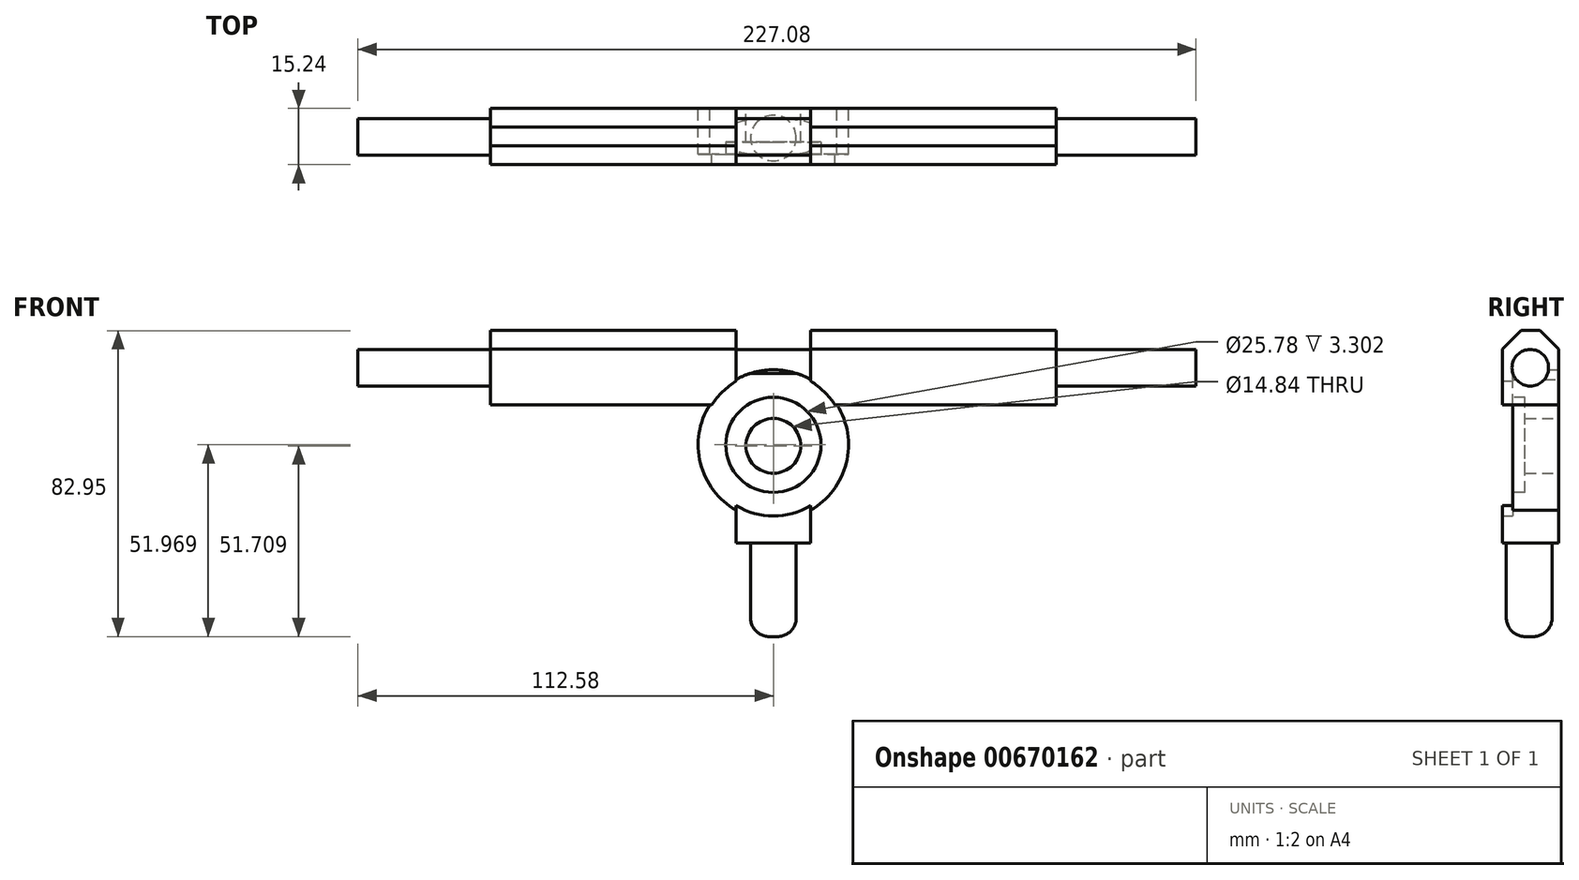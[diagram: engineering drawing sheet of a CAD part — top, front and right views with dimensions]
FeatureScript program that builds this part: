
annotation { "Feature Type Name" : "Feature", "Feature Type Description" : "" }
export const myFeature = defineFeature(function(context is Context, id is Id, definition is map)
    precondition{}
    {
        {
            var Q0;
            Q0=qCreatedBy(makeId("Front.planeOp"),FACE);
            var sketch = newSketch(context, id + "F0", { "sketchPlane" : qUnion([Q0])});
            skLineSegment(sketch, "E0.bottom", {"start": v(-76.65, -10.07) * mm, "end": v(76.65, -10.07) * mm});
            skLineSegment(sketch, "E0.top", {"start": v(-76.65, 10.07) * mm, "end": v(76.65, 10.07) * mm});
            skLineSegment(sketch, "E0.left", {"start": v(-76.65, -10.07) * mm, "end": v(-76.65, 10.07) * mm});
            skLineSegment(sketch, "E0.right", {"start": v(76.65, -10.07) * mm, "end": v(76.65, 10.07) * mm});
            skPoint(sketch, "E0.middle", {"position": v(0, 0) * mm});
            skLineSegment(sketch, "E1.bottom", {"start": v(-10.07, 10.07) * mm, "end": v(10.07, 10.07) * mm});
            skLineSegment(sketch, "E1.top", {"start": v(-10.07, -87.46) * mm, "end": v(10.07, -87.46) * mm});
            skLineSegment(sketch, "E1.left", {"start": v(-10.07, 10.07) * mm, "end": v(-10.07, -87.46) * mm});
            skLineSegment(sketch, "E1.right", {"start": v(10.07, 10.07) * mm, "end": v(10.07, -87.46) * mm});
            skPoint(sketch, "E1.middle", {"position": v(0, -38.7) * mm});
            skArc(sketch, "E2", {"start": v(0, -73.83) * mm, "mid": v(-26.8, -28.1) * mm, "end": v(-76.65, -10.07) * mm});
            skArc(sketch, "E3", {"start": v(76.65, -10.07) * mm, "mid": v(26.8, -28.1) * mm, "end": v(0, -73.83) * mm});
            skLineSegment(sketch, "E4", {"start": v(-10.07, -47.48) * mm, "end": v(10.07, -47.48) * mm});
            skCircle(sketch, "E5", {"center": v(0, -20.52) * mm, "radius": 19.66 * mm});
            skCircle(sketch, "E6", {"center": v(0, -20.52) * mm, "radius": 10.32 * mm});
            skSolve(sketch);
        }
        {
            var Q0;
            {var subQ5=sQuery(id+"F0.wireOp",EDGE,"E0.left");Q0=makeQuery(id+"F0.imprint","IMPRINT",FACE,{"disambiguationData":[TD([[makeQuery(id+"F0.imprint","IMPRINT",EDGE,{"derivedFrom":subQ5}),-1.0]])]});}
            var Q1;
            {var subQ1=sQuery(id+"F0.wireOp",EDGE,"E0.bottom");var subQ3=sQuery(id+"F0.wireOp",EDGE,"E5");var subQ4=makeQuery(id+"F0.imprint","INTERSECT",VERTEX,{"disambiguationData":[OD(0.0)],"derivedFrom":[subQ1,subQ3]});Q1=makeQuery(id+"F0.imprint","IMPRINT",FACE,{"disambiguationData":[TD([[makeQuery(id+"F0.imprint","IMPRINT",EDGE,{"disambiguationData":[TD([[subQ4,-1.0]])],"derivedFrom":subQ3}),-1.0]])]});}
            var Q2;
            {var subQ5=sQuery(id+"F0.wireOp",EDGE,"E0.right");Q2=makeQuery(id+"F0.imprint","IMPRINT",FACE,{"disambiguationData":[TD([[makeQuery(id+"F0.imprint","IMPRINT",EDGE,{"derivedFrom":subQ5}),1.0]])]});}
            var Q3;
            {var subQ1=sQuery(id+"F0.wireOp",EDGE,"E0.bottom");var subQ3=sQuery(id+"F0.wireOp",EDGE,"E5");var subQ4=makeQuery(id+"F0.imprint","INTERSECT",VERTEX,{"disambiguationData":[OD(1.0)],"derivedFrom":[subQ1,subQ3]});Q3=makeQuery(id+"F0.imprint","IMPRINT",FACE,{"disambiguationData":[TD([[makeQuery(id+"F0.imprint","IMPRINT",EDGE,{"disambiguationData":[TD([[subQ4,1.0]])],"derivedFrom":subQ3}),-1.0]])]});}
            var Q4;
            {var subQ0=sQuery(id+"F0.wireOp",EDGE,"E1.bottom");Q4=makeQuery(id+"F0.imprint","IMPRINT",FACE,{"disambiguationData":[TD([[makeQuery(id+"F0.imprint","IMPRINT",EDGE,{"derivedFrom":subQ0}),-1.0]])]});}
            var Q5;
            {var subQ0=sQuery(id+"F0.wireOp",EDGE,"E4");Q5=makeQuery(id+"F0.imprint","IMPRINT",FACE,{"disambiguationData":[TD([[makeQuery(id+"F0.imprint","IMPRINT",EDGE,{"derivedFrom":subQ0}),1.0]])]});}
            extrude(context, id + "F1", {"entities" : qUnion([Q0, Q1, Q2, Q3, Q4, Q5]), "depth" : 15.24 * mm, "offsetDistance" : 25.4 * mm});
        }
        {
            var Q0;
            Q0=makeQuery(id+"F1.opExtrude","SWEPT_FACE",FACE,{"disambiguationData":[OSD([sQuery(id+"F0.wireOp",EDGE,"E4")])]});
            var sketch = newSketch(context, id + "F2", { "sketchPlane" : qUnion([Q0])});
            skCircle(sketch, "E7", {"center": v(0, 8.03) * mm, "radius": 6.2 * mm});
            skSolve(sketch);
        }
        {
            var Q0;
            Q0 = qSketchRegion(id + "F2", true);
            extrude(context, id + "F3", {"entities" : qUnion([Q0]), "operationType" : NewBodyOperationType.ADD, "depth" : 25.4 * mm, "offsetDistance" : 25.4 * mm});
        }
        {
            var Q0;
            Q0=makeQuery(id+"F3.opExtrude","CAP_FACE",FACE,{"disambiguationData":[OSD([sQuery(id+"F2.wireOp",EDGE,"E7")])],"isStart":false});
            fillet(context, id + "F4", {"entities" : qUnion([Q0]), "radius" : 5.08 * mm, "tangentPropagation" : true, "allowEdgeOverflow" : false});
        }
        {
            var Q0;
            Q0=makeQuery(id+"F1.opExtrude","SWEPT_FACE",FACE,{"disambiguationData":[OSD([sQuery(id+"F0.wireOp",EDGE,"E0.right")])]});
            var sketch = newSketch(context, id + "F5", { "sketchPlane" : qUnion([Q0])});
            skCircle(sketch, "E8", {"center": v(-7.74, 0) * mm, "radius": 4.96 * mm});
            skSolve(sketch);
        }
        {
            var Q0;
            Q0=makeQuery(id+"F5.imprint","IMPRINT",FACE,{"disambiguationData":[TD([[makeQuery(id+"F5.imprint","IMPRINT",EDGE,{"derivedFrom":sQuery(id+"F5.wireOp",EDGE,"E8")}),1.0]])]});
            extrude(context, id + "F6", {"entities" : qUnion([Q0]), "depth" : 37.85 * mm, "offsetDistance" : 25.4 * mm, "hasSecondDirection" : true, "secondDirectionOppositeDirection" : true, "secondDirectionDepth" : 189.23 * mm});
        }
        {
            var Q0;
            Q0=qCreatedBy(makeId("Front.planeOp"),FACE);
            var sketch = newSketch(context, id + "F7", { "sketchPlane" : qUnion([Q0])});
            skCircle(sketch, "E9", {"center": v(0, -20.91) * mm, "radius": 20.37 * mm});
            skSolve(sketch);
        }
        {
            var Q0;
            Q0 = qSketchRegion(id + "F7", true);
            extrude(context, id + "F8", {"entities" : qUnion([Q0]), "operationType" : NewBodyOperationType.ADD, "depth" : 12.45 * mm, "offsetDistance" : 25.4 * mm});
        }
        {
            var Q0;
            Q0=makeQuery(id+"F8.opExtrude","CAP_FACE",FACE,{"disambiguationData":[OSD([sQuery(id+"F7.wireOp",EDGE,"E9")])],"isStart":false});
            var sketch = newSketch(context, id + "F9", { "sketchPlane" : qUnion([Q0])});
            skCircle(sketch, "E10", {"center": v(0, -20.91) * mm, "radius": 12.89 * mm});
            skSolve(sketch);
        }
        {
            var Q0;
            Q0 = qSketchRegion(id + "F9", true);
            extrude(context, id + "F10", {"entities" : qUnion([Q0]), "operationType" : NewBodyOperationType.REMOVE, "oppositeDirection" : true, "depth" : 7.87 * mm, "offsetDistance" : 25.4 * mm});
        }
        {
            var Q0;
            Q0=makeQuery(id+"F8.opExtrude","CAP_FACE",FACE,{"disambiguationData":[OSD([sQuery(id+"F7.wireOp",EDGE,"E9")])],"isStart":true});
            var sketch = newSketch(context, id + "F11", { "sketchPlane" : qUnion([Q0])});
            skCircle(sketch, "E11", {"center": v(0, -20.91) * mm, "radius": 13.15 * mm});
            skSolve(sketch);
        }
        {
            var Q0;
            Q0=makeQuery(id+"F11.imprint","IMPRINT",FACE,{"disambiguationData":[TD([[makeQuery(id+"F11.imprint","IMPRINT",EDGE,{"derivedFrom":sQuery(id+"F11.wireOp",EDGE,"E11")}),1.0]])]});
            extrude(context, id + "F12", {"entities" : qUnion([Q0]), "operationType" : NewBodyOperationType.REMOVE, "oppositeDirection" : true, "depth" : 5.08 * mm, "offsetDistance" : 25.4 * mm});
        }
        {
            var Q0;
            Q0=qCreatedBy(makeId("Front.planeOp"),FACE);
            var sketch = newSketch(context, id + "F13", { "sketchPlane" : qUnion([Q0])});
            skCircle(sketch, "E12", {"center": v(0, -21.17) * mm, "radius": 7.42 * mm});
            skSolve(sketch);
        }
        {
            var Q0;
            Q0=makeQuery(id+"F13.imprint","IMPRINT",FACE,{"disambiguationData":[TD([[makeQuery(id+"F13.imprint","IMPRINT",EDGE,{"derivedFrom":sQuery(id+"F13.wireOp",EDGE,"E12")}),1.0]])]});
            var sketch = newSketch(context, id + "F14", { "sketchPlane" : qUnion([Q0])});
            skCircle(sketch, "E13", {"center": v(0, -20.59) * mm, "radius": 14.96 * mm});
            skSolve(sketch);
        }
        {
            var Q0;
            Q0 = qSketchRegion(id + "F14", true);
            var Q1;
            Q1=makeQuery(id+"F13.imprint","IMPRINT",FACE,{"disambiguationData":[TD([[makeQuery(id+"F13.imprint","IMPRINT",EDGE,{"derivedFrom":sQuery(id+"F13.wireOp",EDGE,"E12")}),1.0]])]});
            extrude(context, id + "F15", {"entities" : qUnion([Q0, Q1]), "operationType" : NewBodyOperationType.ADD, "depth" : 9.14 * mm, "offsetDistance" : 25.4 * mm});
        }
        {
            var Q0;
            Q0 = qSketchRegion(id + "F13", true);
            extrude(context, id + "F16", {"entities" : qUnion([Q0]), "operationType" : NewBodyOperationType.REMOVE, "depth" : 47.75 * mm, "offsetDistance" : 25.4 * mm});
        }
        {
            var Q0;
            Q0=makeQuery(id+"F1.opExtrude","CAP_EDGE",EDGE,{"disambiguationData":[OSD([sQuery(id+"F0.wireOp",EDGE,"E0.top"),sQuery(id+"F0.wireOp",EDGE,"E1.bottom")])],"isStart":false});
            var Q1;
            Q1=makeQuery(id+"F1.opExtrude","CAP_EDGE",EDGE,{"disambiguationData":[OSD([sQuery(id+"F0.wireOp",EDGE,"E2")])],"isStart":false});
            var Q2;
            Q2=makeQuery(id+"F1.opExtrude","CAP_EDGE",EDGE,{"disambiguationData":[OSD([sQuery(id+"F0.wireOp",EDGE,"E3")])],"isStart":false});
            var Q3;
            Q3=makeQuery(id+"F1.opExtrude","CAP_EDGE",EDGE,{"disambiguationData":[OSD([sQuery(id+"F0.wireOp",EDGE,"E3")])],"isStart":true});
            var Q4;
            Q4=makeQuery(id+"F1.opExtrude","CAP_EDGE",EDGE,{"disambiguationData":[OSD([sQuery(id+"F0.wireOp",EDGE,"E2")])],"isStart":true});
            var Q5;
            Q5=makeQuery(id+"F1.opExtrude","CAP_EDGE",EDGE,{"disambiguationData":[OSD([sQuery(id+"F0.wireOp",EDGE,"E0.top"),sQuery(id+"F0.wireOp",EDGE,"E1.bottom")])],"isStart":true});
            chamfer(context, id + "F17", {"entities" : qUnion([Q0, Q1, Q2, Q3, Q4, Q5]), "width" : 5.08 * mm, "tangentPropagation" : true});
        }
    });
